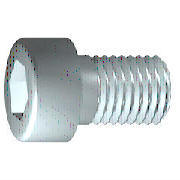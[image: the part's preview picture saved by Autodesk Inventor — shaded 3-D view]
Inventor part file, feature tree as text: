
AUTODESK INVENTOR PART (.ipt)
format: ipt  version: 2022 (Build 260153000, 153)  size: 196,096 bytes
history: native  units: mm (DEFAULTED — no unit token found)
features: sketch x2, extrude x1, plane x1, fillet x1
ambient origin geometry x7: Origin, YZ Plane, XY Plane, X Axis, Y Axis, Z Axis, Center Point
bodies: Solid1 (feature_tree), Body (feature_tree)
feature tree (5):
  extrude  "Slot"  Depth=4.0mm
  plane  "Work Plane1"
  fillet  "Fillet2"  Radius=4.0mm
  sketch  "Sketch1"  dims[d1=6.25mm d2=0.429515mm d3=4.0mm]
  sketch  "Sketch2"  dims[d4=2.0mm d5=60.0deg d6=4.0mm d7=4.0mm d8=3.464102mm d9=7.0mm d10=90.0deg d11=10.0mm d12=0.0mm d13=6.25mm d14=0.0mm d15=0.429415mm d16=0.429415mm d17=0.4mm d19=0.0mm d26=8.0mm d27=45.0deg d28=0.0mm d29=0.0mm d30=0.1mm]
